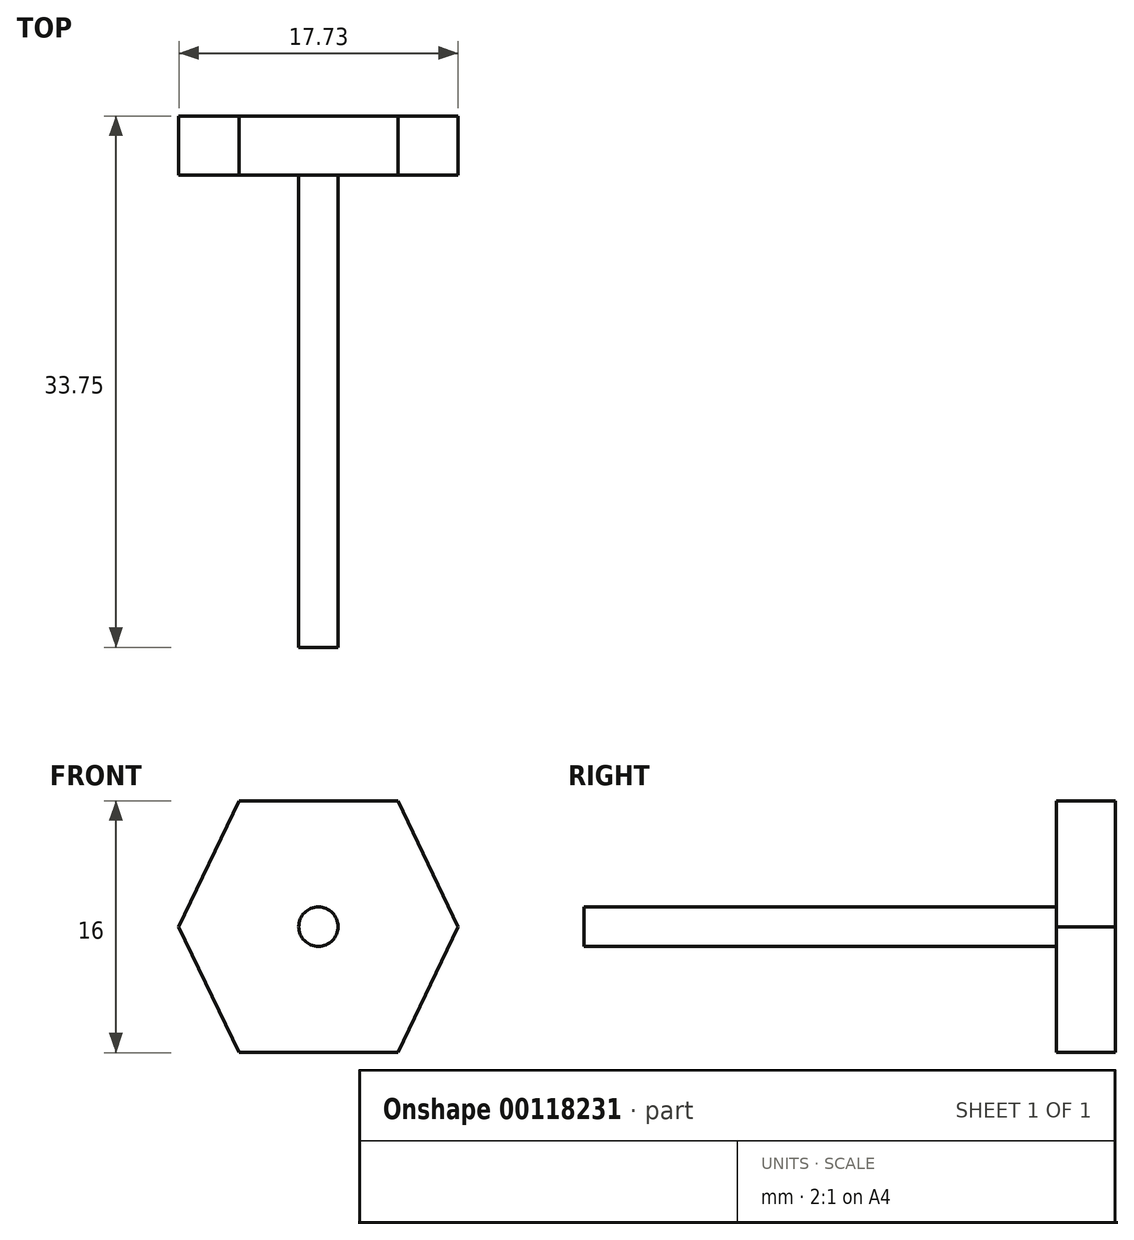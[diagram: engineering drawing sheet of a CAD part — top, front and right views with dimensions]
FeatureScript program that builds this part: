
annotation { "Feature Type Name" : "Feature", "Feature Type Description" : "" }
export const myFeature = defineFeature(function(context is Context, id is Id, definition is map)
    precondition{}
    {
        {
            var Q0;
            Q0=qCreatedBy(makeId("Front.planeOp"),FACE);
            var sketch = newSketch(context, id + "F0", { "sketchPlane" : qUnion([Q0])});
            skLineSegment(sketch, "E0", {"start": v(-3.68, 25.15) * mm, "end": v(6.4, 25.15) * mm});
            skLineSegment(sketch, "E1", {"start": v(6.4, 25.15) * mm, "end": v(10.23, 17.15) * mm});
            skLineSegment(sketch, "E2", {"start": v(10.23, 17.15) * mm, "end": v(6.4, 9.15) * mm});
            skLineSegment(sketch, "E3", {"start": v(6.4, 9.15) * mm, "end": v(-3.68, 9.15) * mm});
            skLineSegment(sketch, "E4", {"start": v(-3.68, 9.15) * mm, "end": v(-7.5, 17.15) * mm});
            skLineSegment(sketch, "E5", {"start": v(-7.5, 17.15) * mm, "end": v(-3.68, 25.15) * mm});
            skSolve(sketch);
        }
        {
            var Q0;
            Q0 = qSketchRegion(id + "F0", true);
            extrude(context, id + "F1", {"entities" : qUnion([Q0]), "depth" : 3.75 * mm});
        }
        {
            var Q0;
            Q0=makeQuery(id+"F1.opExtrude","CAP_FACE",FACE,{"disambiguationData":[OSD([sQuery(id+"F0.wireOp",EDGE,"E0"),sQuery(id+"F0.wireOp",EDGE,"E1"),sQuery(id+"F0.wireOp",EDGE,"E2"),sQuery(id+"F0.wireOp",EDGE,"E3"),sQuery(id+"F0.wireOp",EDGE,"E4"),sQuery(id+"F0.wireOp",EDGE,"E5")])],"isStart":false});
            var sketch = newSketch(context, id + "F2", { "sketchPlane" : qUnion([Q0])});
            skPoint(sketch, "E6", {"position": v(1.36, 17.15) * mm});
            skCircle(sketch, "E7", {"center": v(1.36, 17.15) * mm, "radius": 1.25 * mm});
            skSolve(sketch);
        }
        {
            var Q0;
            Q0 = qSketchRegion(id + "F2", true);
            extrude(context, id + "F3", {"entities" : qUnion([Q0]), "operationType" : NewBodyOperationType.ADD, "depth" : 30 * mm});
        }
    });
